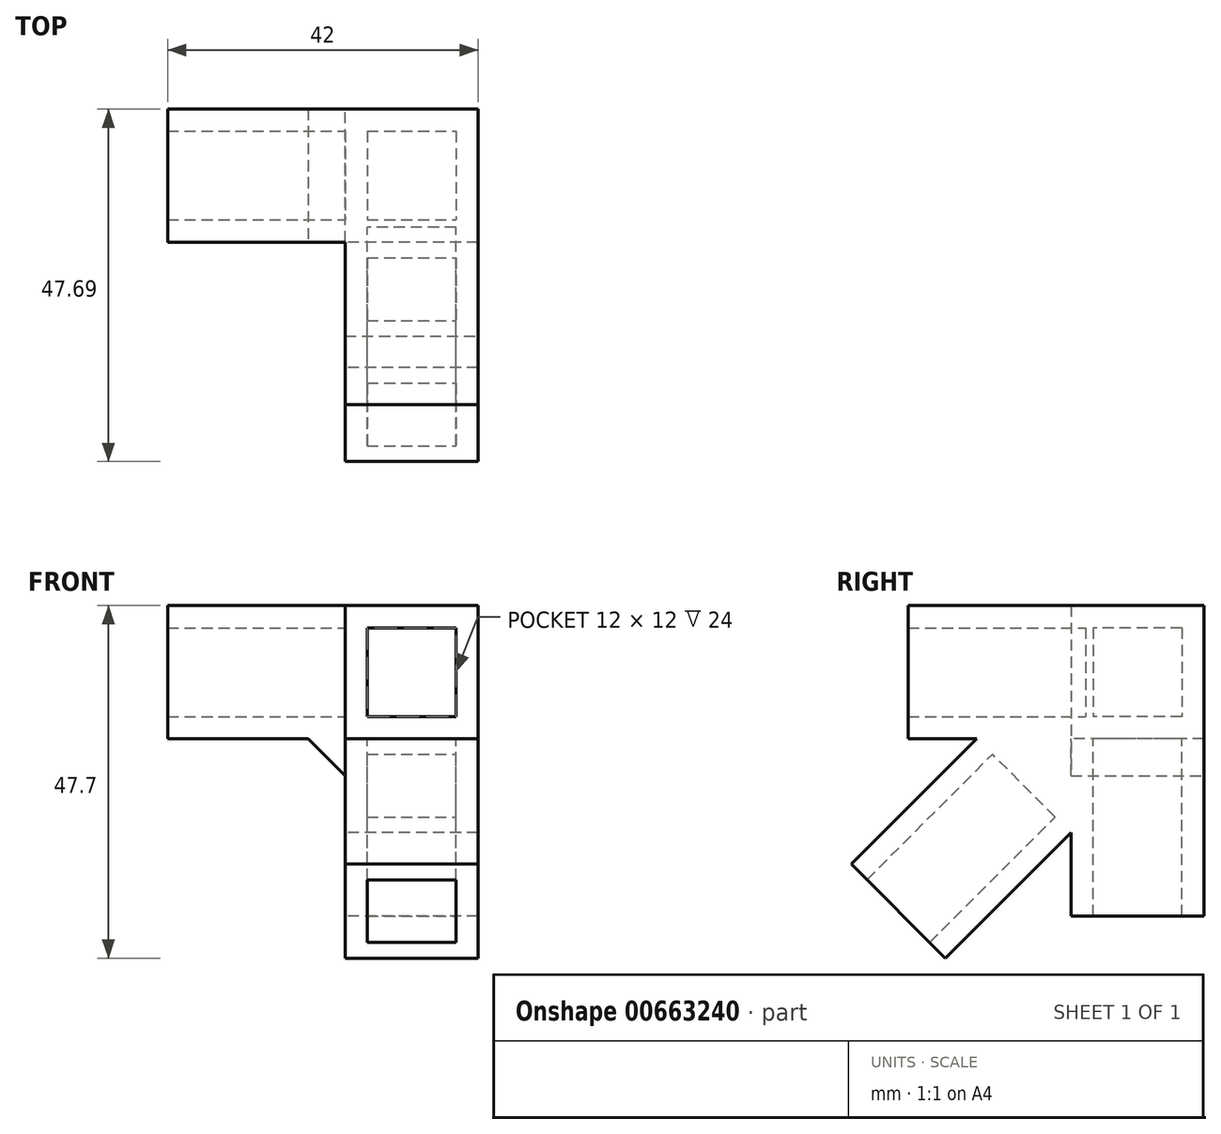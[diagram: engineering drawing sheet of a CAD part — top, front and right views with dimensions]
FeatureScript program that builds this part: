
annotation { "Feature Type Name" : "Feature", "Feature Type Description" : "" }
export const myFeature = defineFeature(function(context is Context, id is Id, definition is map)
    precondition{}
    {
        {
            var Q0;
            Q0=qCreatedBy(makeId("Front.planeOp"),FACE);
            var sketch = newSketch(context, id + "F0", { "sketchPlane" : qUnion([Q0])});
            skLineSegment(sketch, "E0.bottom", {"start": v(6, 6) * mm, "end": v(-6, 6) * mm});
            skLineSegment(sketch, "E0.top", {"start": v(6, -6) * mm, "end": v(-6, -6) * mm});
            skLineSegment(sketch, "E0.left", {"start": v(6, 6) * mm, "end": v(6, -6) * mm});
            skLineSegment(sketch, "E0.right", {"start": v(-6, 6) * mm, "end": v(-6, -6) * mm});
            skPoint(sketch, "E0.middle", {"position": v(0, 0) * mm});
            skLineSegment(sketch, "E1.0", {"start": v(9, 9) * mm, "end": v(-9, 9) * mm});
            skLineSegment(sketch, "E1.1", {"start": v(9, 9) * mm, "end": v(9, -9) * mm});
            skLineSegment(sketch, "E1.2", {"start": v(9, -9) * mm, "end": v(-9, -9) * mm});
            skLineSegment(sketch, "E1.3", {"start": v(-9, 9) * mm, "end": v(-9, -9) * mm});
            skSolve(sketch);
        }
        {
            var Q0;
            Q0=makeQuery(id+"F0.imprint","IMPRINT",FACE,{"disambiguationData":[TD([[makeQuery(id+"F0.imprint","IMPRINT",EDGE,{"derivedFrom":sQuery(id+"F0.wireOp",EDGE,"E0.bottom")}),-1.0]])]});
            extrude(context, id + "F1", {"entities" : qUnion([Q0]), "depth" : 32 * mm, "offsetDistance" : 25 * mm});
        }
        {
            var Q0;
            Q0=makeQuery(id+"F1.opExtrude","SWEPT_FACE",FACE,{"disambiguationData":[OSD([sQuery(id+"F0.wireOp",EDGE,"E1.0")])]});
            var sketch = newSketch(context, id + "F2", { "sketchPlane" : qUnion([Q0])});
            skLineSegment(sketch, "E2.bottom", {"start": v(9, -8.01) * mm, "end": v(-9, -8.01) * mm});
            skLineSegment(sketch, "E2.top", {"start": v(9, 8.01) * mm, "end": v(-9, 8.01) * mm});
            skLineSegment(sketch, "E2.left", {"start": v(9, -8.01) * mm, "end": v(9, 8.01) * mm});
            skLineSegment(sketch, "E2.right", {"start": v(-9, 0) * mm, "end": v(-9, 8.01) * mm});
            skPoint(sketch, "E2.middle", {"position": v(0, 0) * mm});
            skLineSegment(sketch, "E3", {"start": v(9, 0) * mm, "end": v(-9, 0) * mm});
            skSolve(sketch);
        }
        {
            var Q0;
            Q0=qSketchRegion(id+"F2",true);
            var Q1;
            Q1=makeQuery(id+"F1.opExtrude","SWEPT_FACE",FACE,{"disambiguationData":[OSD([sQuery(id+"F0.wireOp",EDGE,"E1.2")])]});
            extrude(context, id + "F3", {"entities" : qUnion([Q0]), "operationType" : NewBodyOperationType.ADD, "endBound" : BoundingType.UP_TO_SURFACE, "oppositeDirection" : true, "depth" : 25 * mm, "endBoundEntityFace" : qUnion([Q1]), "offsetDistance" : 25 * mm});
        }
        {
            var Q0;
            {var subQ0=sQuery(id+"F0.wireOp",EDGE,"E1.2");Q0=makeQuery(id+"F3.boolean.opBoolean","MERGE",FACE,{"derivedFrom":[makeQuery(id+"F1.opExtrude","SWEPT_FACE",FACE,{"disambiguationData":[OSD([subQ0])]}),makeQuery(id+"F3.opExtrude","CAP_FACE",FACE,{"disambiguationData":[OSD([subQ0])],"isStart":false})]});}
            var sketch = newSketch(context, id + "F4", { "sketchPlane" : qUnion([Q0])});
            skLineSegment(sketch, "E4.bottom", {"start": v(-9, -8.01) * mm, "end": v(9, -8.01) * mm});
            skLineSegment(sketch, "E4.top", {"start": v(-9, 9.99) * mm, "end": v(9, 9.99) * mm});
            skLineSegment(sketch, "E4.left", {"start": v(-9, -8.01) * mm, "end": v(-9, 9.99) * mm});
            skLineSegment(sketch, "E4.right", {"start": v(9, -8.01) * mm, "end": v(9, 9.99) * mm});
            skLineSegment(sketch, "E5.0", {"start": v(-6, 6.99) * mm, "end": v(6, 6.99) * mm});
            skLineSegment(sketch, "E5.1", {"start": v(-6, -5.01) * mm, "end": v(-6, 6.99) * mm});
            skLineSegment(sketch, "E5.2", {"start": v(-6, -5.01) * mm, "end": v(6, -5.01) * mm});
            skLineSegment(sketch, "E5.3", {"start": v(6, -5.01) * mm, "end": v(6, 6.99) * mm});
            skSolve(sketch);
        }
        {
            var Q0;
            Q0=qSketchRegion(id+"F4",true);
            extrude(context, id + "F5", {"entities" : qUnion([Q0]), "operationType" : NewBodyOperationType.ADD, "depth" : 24 * mm, "offsetDistance" : 25 * mm});
        }
        {
            var Q0;
            Q0=makeQuery(id+"F5.boolean.opBoolean","MERGE",FACE,{"derivedFrom":[makeQuery(id+"F3.boolean.opBoolean","MERGE",FACE,{"derivedFrom":[makeQuery(id+"F1.opExtrude","SWEPT_FACE",FACE,{"disambiguationData":[OSD([sQuery(id+"F0.wireOp",EDGE,"E1.3")])]}),makeQuery(id+"F3.opExtrude","SWEPT_FACE",FACE,{"disambiguationData":[OSD([sQuery(id+"F2.wireOp",EDGE,"E2.right")])]})]}),makeQuery(id+"F5.opExtrude","SWEPT_FACE",FACE,{"disambiguationData":[OSD([sQuery(id+"F4.wireOp",EDGE,"E4.left")])]})]});
            var sketch = newSketch(context, id + "F6", { "sketchPlane" : qUnion([Q0])});
            skLineSegment(sketch, "E6.bottom", {"start": v(-8.01, 9) * mm, "end": v(9.99, 9) * mm});
            skLineSegment(sketch, "E6.top", {"start": v(-8.01, -9) * mm, "end": v(9.99, -9) * mm});
            skLineSegment(sketch, "E6.left", {"start": v(-8.01, 9) * mm, "end": v(-8.01, -9) * mm});
            skLineSegment(sketch, "E6.right", {"start": v(9.99, 9) * mm, "end": v(9.99, -9) * mm});
            skLineSegment(sketch, "E7.0", {"start": v(6.99, 6) * mm, "end": v(6.99, -6) * mm});
            skLineSegment(sketch, "E7.1", {"start": v(-5.01, 6) * mm, "end": v(6.99, 6) * mm});
            skLineSegment(sketch, "E7.2", {"start": v(-5.01, 6) * mm, "end": v(-5.01, -6) * mm});
            skLineSegment(sketch, "E7.3", {"start": v(-5.01, -6) * mm, "end": v(6.99, -6) * mm});
            skSolve(sketch);
        }
        {
            var Q0;
            Q0=makeQuery(id+"F6.imprint","IMPRINT",FACE,{"disambiguationData":[TD([[makeQuery(id+"F6.imprint","IMPRINT",EDGE,{"derivedFrom":sQuery(id+"F6.wireOp",EDGE,"E6.bottom")}),1.0]])]});
            extrude(context, id + "F7", {"entities" : qUnion([Q0]), "operationType" : NewBodyOperationType.ADD, "depth" : 24 * mm, "offsetDistance" : 25 * mm});
        }
        {
            var Q0;
            Q0=makeQuery(id+"F5.opExtrude","CAP_EDGE",EDGE,{"disambiguationData":[OSD([sQuery(id+"F4.wireOp",EDGE,"E4.top")])],"isStart":true});
            chamfer(context, id + "F8", {"entities" : qUnion([Q0]), "width" : 12.73 * mm, "tangentPropagation" : true});
        }
        {
            var Q0;
            Q0=makeQuery(id+"F8.opChamfer","BLEND_FACE",FACE,{"disambiguationData":[OSD([sQuery(id+"F4.wireOp",EDGE,"E4.top")])]});
            var sketch = newSketch(context, id + "F9", { "sketchPlane" : qUnion([Q0])});
            skLineSegment(sketch, "E8.bottom", {"start": v(-9, -8.3) * mm, "end": v(9, -8.3) * mm});
            skLineSegment(sketch, "E8.top", {"start": v(-9, 9.7) * mm, "end": v(9, 9.7) * mm});
            skLineSegment(sketch, "E8.left", {"start": v(-9, -8.3) * mm, "end": v(-9, 9.7) * mm});
            skLineSegment(sketch, "E8.right", {"start": v(9, -8.3) * mm, "end": v(9, 9.7) * mm});
            skLineSegment(sketch, "E9.0", {"start": v(-6, -5.3) * mm, "end": v(-6, 6.7) * mm});
            skLineSegment(sketch, "E9.1", {"start": v(-6, -5.3) * mm, "end": v(6, -5.3) * mm});
            skLineSegment(sketch, "E9.2", {"start": v(6, -5.3) * mm, "end": v(6, 6.7) * mm});
            skLineSegment(sketch, "E9.3", {"start": v(-6, 6.7) * mm, "end": v(6, 6.7) * mm});
            skSolve(sketch);
        }
        {
            var Q0;
            Q0=qSketchRegion(id+"F9",true);
            extrude(context, id + "F10", {"entities" : qUnion([Q0]), "operationType" : NewBodyOperationType.ADD, "depth" : 24 * mm, "offsetDistance" : 25 * mm});
        }
        {
            var Q0;
            Q0=makeQuery(id+"F7.opExtrude","CAP_EDGE",EDGE,{"disambiguationData":[OSD([sQuery(id+"F6.wireOp",EDGE,"E6.top")])],"isStart":true});
            var Q1;
            Q1=makeQuery(id+"F7.opExtrude","CAP_EDGE",EDGE,{"disambiguationData":[OSD([sQuery(id+"F6.wireOp",EDGE,"E6.right")])],"isStart":true});
            chamfer(context, id + "F11", {"entities" : qUnion([Q0, Q1]), "width" : 5 * mm, "tangentPropagation" : true});
        }
        {
            var Q0;
            Q0=makeQuery(id+"F3.opExtrude","SWEPT_FACE",FACE,{"disambiguationData":[OSD([sQuery(id+"F2.wireOp",EDGE,"E3")])]});
            var sketch = newSketch(context, id + "F12", { "sketchPlane" : qUnion([Q0])});
            skLineSegment(sketch, "E10.bottom", {"start": v(-6, -6) * mm, "end": v(6, -6) * mm});
            skLineSegment(sketch, "E10.top", {"start": v(-6, 6) * mm, "end": v(6, 6) * mm});
            skLineSegment(sketch, "E10.left", {"start": v(-6, -6) * mm, "end": v(-6, 6) * mm});
            skLineSegment(sketch, "E10.right", {"start": v(6, -6) * mm, "end": v(6, 6) * mm});
            skPoint(sketch, "E10.middle", {"position": v(0, 0) * mm});
            skSolve(sketch);
        }
        {
            var Q0;
            Q0=makeQuery(id+"F12.imprint","IMPRINT",FACE,{"disambiguationData":[TD([[makeQuery(id+"F12.imprint","IMPRINT",EDGE,{"derivedFrom":sQuery(id+"F12.wireOp",EDGE,"E10.bottom")}),-1.0]])]});
            extrude(context, id + "F13", {"entities" : qUnion([Q0]), "operationType" : NewBodyOperationType.ADD, "depth" : 8 * mm, "offsetDistance" : 25 * mm});
        }
    });
